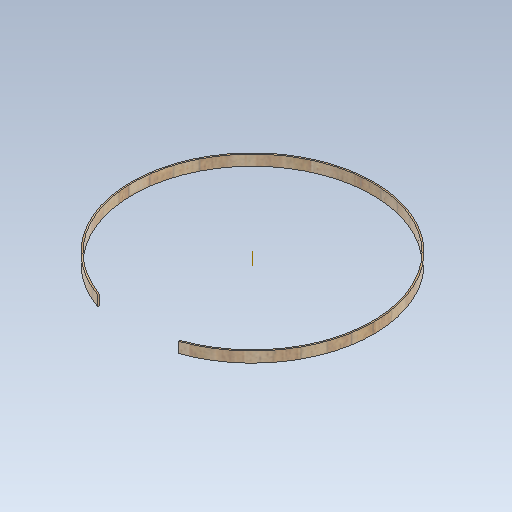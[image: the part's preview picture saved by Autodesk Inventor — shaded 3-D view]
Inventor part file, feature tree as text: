
AUTODESK INVENTOR PART (.ipt)
format: ipt  version: 2020 (Build 240168000, 168)  size: 199,168 bytes
history: native  units: mm
features: extrude x2, sketch x1
ambient origin geometry x8: Origin, YZ Plane, XZ Plane, XY Plane, X Axis, Y Axis, Z Axis, Center Point
bodies: Body1 (feature_tree)
feature tree (3):
  extrude  "Extrusion3"  Depth=345.36mm
  extrude  "Extrusion5"  Depth=345.36mm
  sketch  "Sketch3"  dims[d15=30.0mm d16=0.0mm d40=3.25mm d52=4.363323mm d54=10.0mm d55=0.0mm d60=0.872665mm d61=12.566371mm d62=13.439035mm d85=682.72mm d87=150.07mm d88=345.36mm d89=4.363323mm d90=1.919862mm d91=1.919862mm d169=690.72mm]
